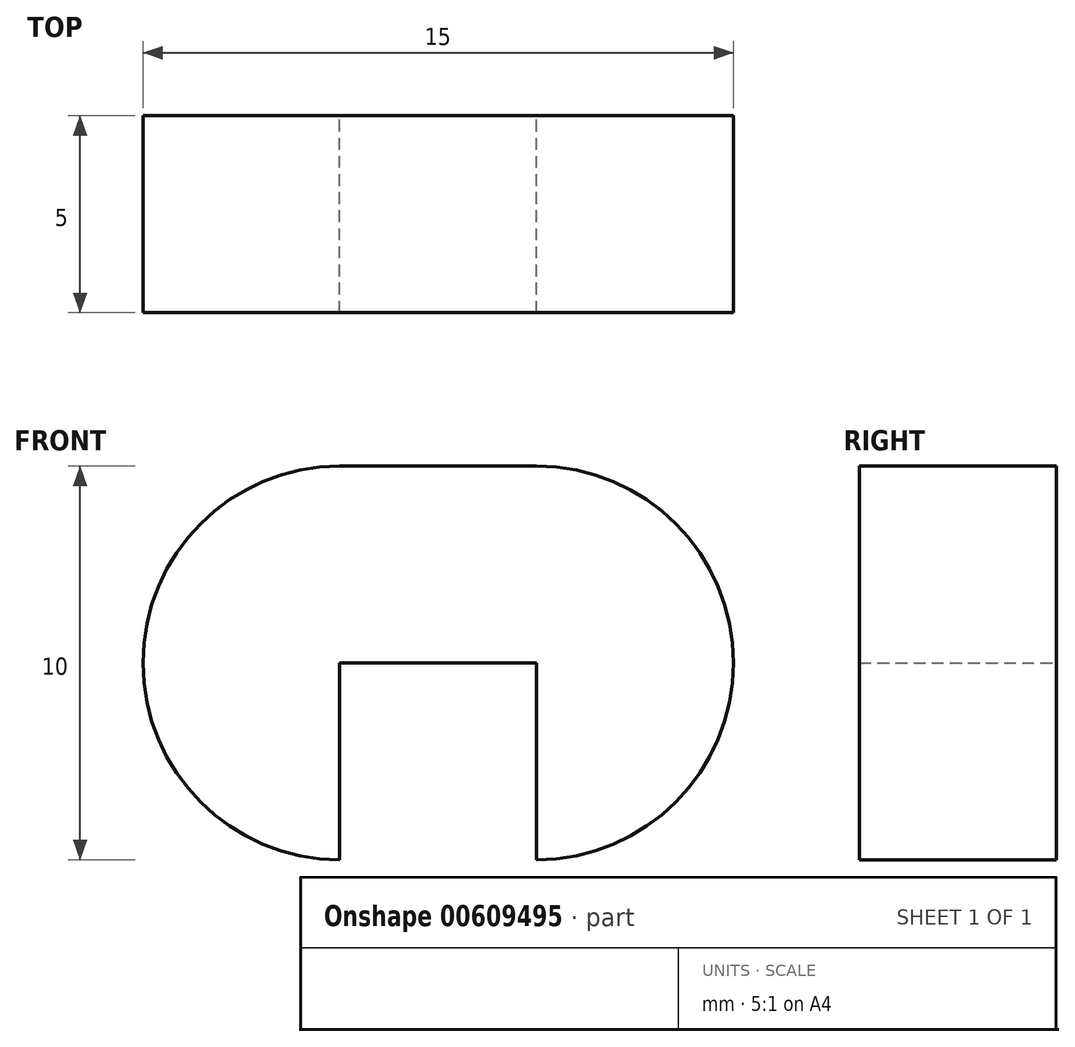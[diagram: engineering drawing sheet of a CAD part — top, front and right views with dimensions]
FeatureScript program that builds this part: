
annotation { "Feature Type Name" : "Feature", "Feature Type Description" : "" }
export const myFeature = defineFeature(function(context is Context, id is Id, definition is map)
    precondition{}
    {
        {
            var Q0;
            Q0=qCreatedBy(makeId("Front.planeOp"),FACE);
            var sketch = newSketch(context, id + "F0", { "sketchPlane" : qUnion([Q0])});
            skLineSegment(sketch, "E0", {"start": v(0, 0) * mm, "end": v(0, 5) * mm});
            skLineSegment(sketch, "E1", {"start": v(0, 5) * mm, "end": v(5, 5) * mm});
            skLineSegment(sketch, "E2", {"start": v(5, 5) * mm, "end": v(5, 0) * mm});
            skLineSegment(sketch, "E3", {"start": v(5, 0) * mm, "end": v(10, 0) * mm});
            skLineSegment(sketch, "E4", {"start": v(10, 0) * mm, "end": v(10, 10) * mm});
            skLineSegment(sketch, "E5", {"start": v(10, 10) * mm, "end": v(-5, 10) * mm});
            skLineSegment(sketch, "E6", {"start": v(-5, 10) * mm, "end": v(-5, 0) * mm});
            skLineSegment(sketch, "E7", {"start": v(-5, 0) * mm, "end": v(0, 0) * mm});
            skSolve(sketch);
        }
        {
            var Q0;
            Q0 = qSketchRegion(id + "F0", true);
            extrude(context, id + "F1", {"entities" : qUnion([Q0]), "depth" : 5 * mm, "offsetDistance" : 25 * mm});
        }
        {
            var Q0;
            Q0=makeQuery(id+"F1.opExtrude","SWEPT_EDGE",EDGE,{"disambiguationData":[OSD([sQuery(id+"F0.wireOp",EDGE,"E4"),sQuery(id+"F0.wireOp",EDGE,"E5")])]});
            var Q1;
            Q1=makeQuery(id+"F1.opExtrude","SWEPT_EDGE",EDGE,{"disambiguationData":[OSD([sQuery(id+"F0.wireOp",EDGE,"E3"),sQuery(id+"F0.wireOp",EDGE,"E4")])]});
            var Q2;
            Q2=makeQuery(id+"F1.opExtrude","SWEPT_EDGE",EDGE,{"disambiguationData":[OSD([sQuery(id+"F0.wireOp",EDGE,"E5"),sQuery(id+"F0.wireOp",EDGE,"E6")])]});
            var Q3;
            Q3=makeQuery(id+"F1.opExtrude","SWEPT_EDGE",EDGE,{"disambiguationData":[OSD([sQuery(id+"F0.wireOp",EDGE,"E6"),sQuery(id+"F0.wireOp",EDGE,"E7")])]});
            fillet(context, id + "F2", {"entities" : qUnion([Q0, Q1, Q2, Q3]), "radius" : 5 * mm, "tangentPropagation" : true, "allowEdgeOverflow" : false});
        }
    });
